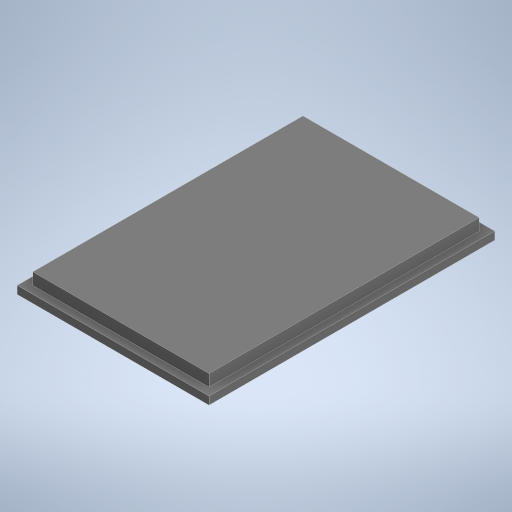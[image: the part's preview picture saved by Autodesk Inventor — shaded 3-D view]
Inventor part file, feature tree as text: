
AUTODESK INVENTOR PART (.ipt)
format: ipt  version: 2023 (Build 270158000, 158)  size: 219,136 bytes
history: native  units: in
note: dims shown in document units (in); Inventor stores cm internally (conversion verified against a paired STEP export)
features: extrude x2, sketch x1
ambient origin geometry x8: Origin, YZ Plane, XZ Plane, XY Plane, X Axis, Y Axis, Z Axis, Center Point
bodies: Solid1 (feature_tree)
feature tree (3):
  sketch  "Sketch1"  dims[d0=2.25in d1=3.45in d2=0.1in d3=0.25in d4=0.0in d5=0.1in d6=0.0in]
  extrude  "Extrusion1"  Depth=3.45in
  extrude  "Extrusion2"  Depth=0.1in
